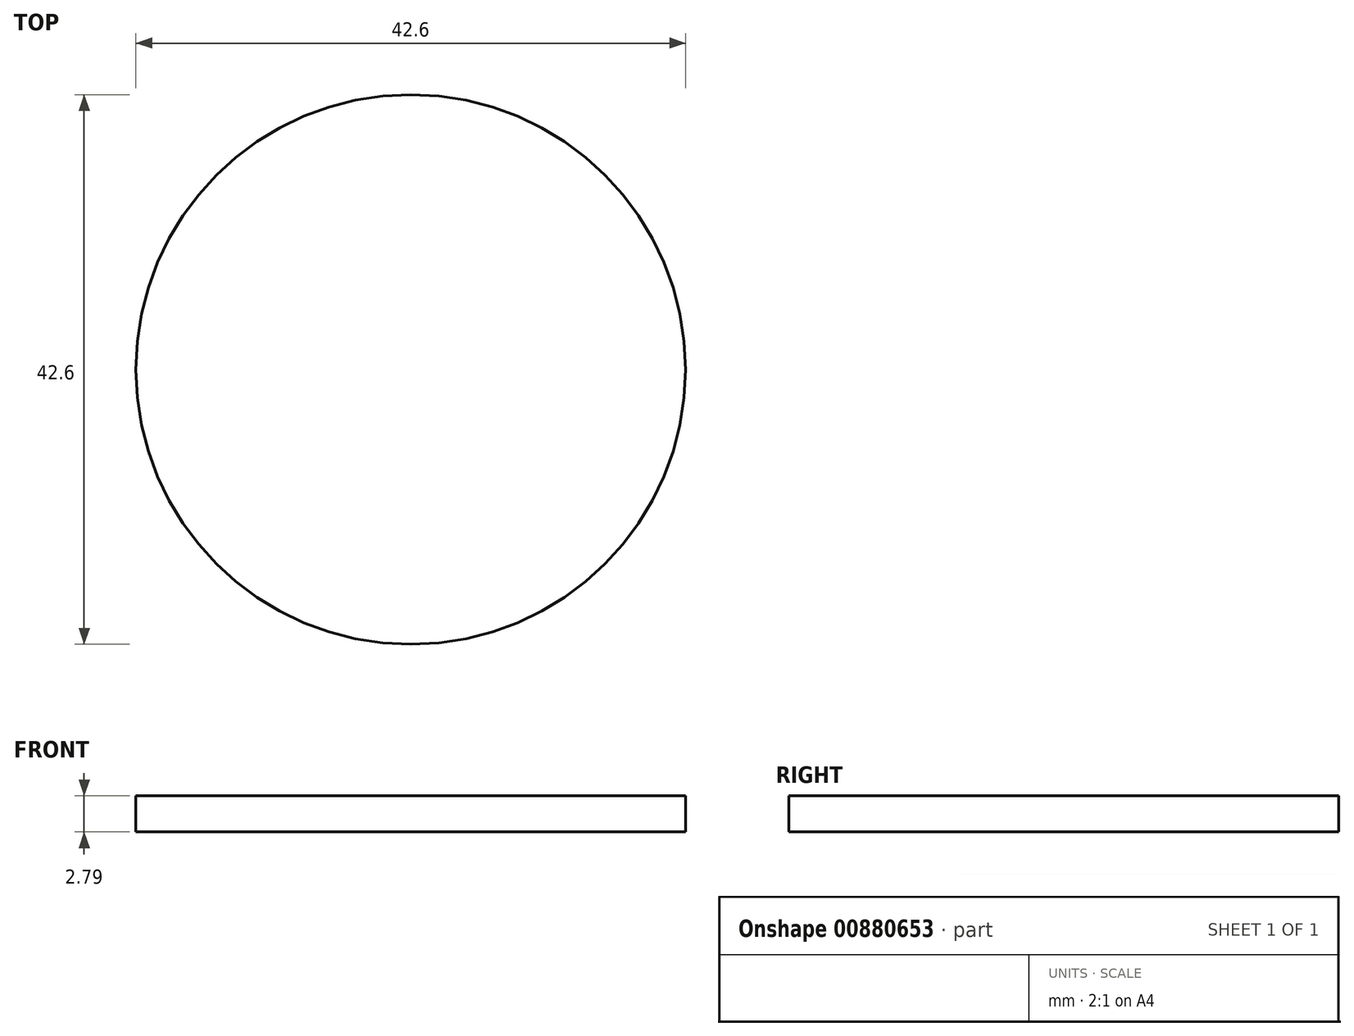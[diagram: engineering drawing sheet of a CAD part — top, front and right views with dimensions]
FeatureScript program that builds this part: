
annotation { "Feature Type Name" : "Feature", "Feature Type Description" : "" }
export const myFeature = defineFeature(function(context is Context, id is Id, definition is map)
    precondition{}
    {
        {
            var Q0;
            Q0=qCreatedBy(makeId("Top.planeOp"),FACE);
            var sketch = newSketch(context, id + "F0", { "sketchPlane" : qUnion([Q0])});
            skCircle(sketch, "E0", {"center": v(0, 0) * mm, "radius": 21.3 * mm});
            skSolve(sketch);
        }
        {
            var Q0;
            Q0=makeQuery(id+"F0.imprint","IMPRINT",FACE,{"disambiguationData":[TD([[makeQuery(id+"F0.imprint","IMPRINT",EDGE,{"derivedFrom":sQuery(id+"F0.wireOp",EDGE,"E0")}),1.0]])]});
            extrude(context, id + "F1", {"entities" : qUnion([Q0]), "depth" : 2.8 * mm, "offsetDistance" : 25.4 * mm});
        }
    });
